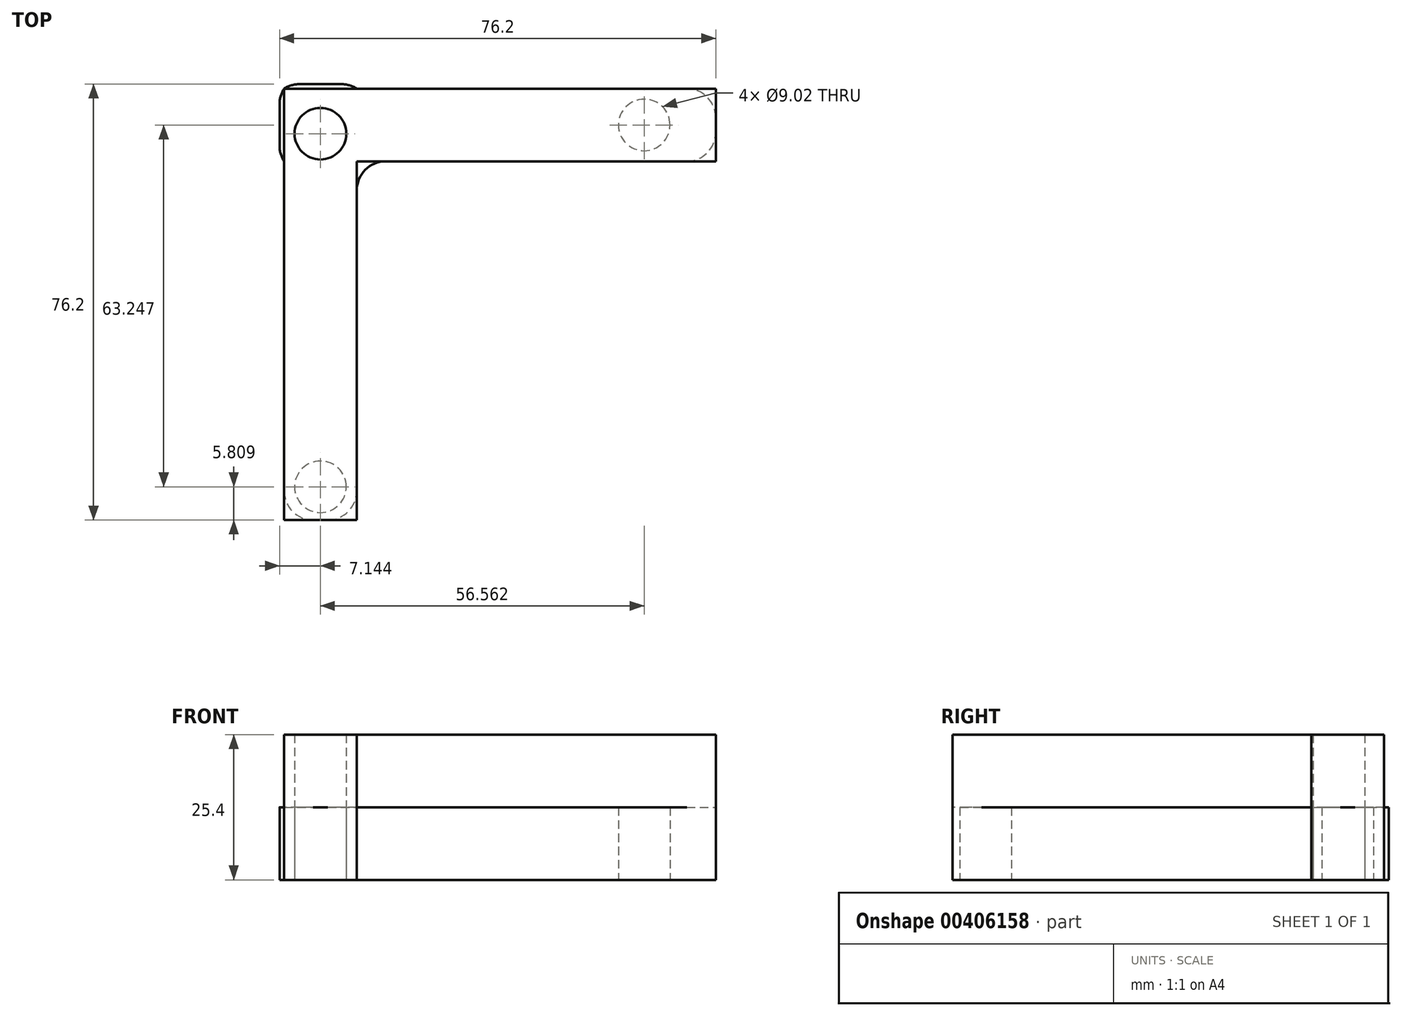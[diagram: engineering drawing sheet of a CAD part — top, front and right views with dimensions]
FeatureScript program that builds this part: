
annotation { "Feature Type Name" : "Feature", "Feature Type Description" : "" }
export const myFeature = defineFeature(function(context is Context, id is Id, definition is map)
    precondition{}
    {
        {
            var Q0;
            Q0=qCreatedBy(makeId("Top.planeOp"),FACE);
            var sketch = newSketch(context, id + "F0", { "sketchPlane" : qUnion([Q0])});
            skLineSegment(sketch, "E0.bottom", {"start": v(-24.6, -38.1) * mm, "end": v(-37.3, -38.1) * mm});
            skLineSegment(sketch, "E0.top", {"start": v(-24.6, 38.1) * mm, "end": v(-37.3, 38.1) * mm});
            skLineSegment(sketch, "E0.left", {"start": v(-24.6, -38.1) * mm, "end": v(-24.6, 24.6) * mm});
            skLineSegment(sketch, "E0.right", {"start": v(-37.3, -38.1) * mm, "end": v(-37.3, 38.1) * mm});
            skPoint(sketch, "E0.middle", {"position": v(-30.96, 0) * mm});
            skLineSegment(sketch, "E1.MirrorCS", {"start": v(38.1, 24.6) * mm, "end": v(-24.6, 24.6) * mm});
            skLineSegment(sketch, "E2.MirrorCS", {"start": v(-38.1, 24.6) * mm, "end": v(-38.1, 37.3) * mm});
            skLineSegment(sketch, "E3.MirrorCS", {"start": v(38.1, 24.6) * mm, "end": v(38.1, 37.3) * mm});
            skLineSegment(sketch, "E4.MirrorCS", {"start": v(38.1, 37.3) * mm, "end": v(-38.1, 37.3) * mm});
            skLineSegment(sketch, "E5.trimOffspring", {"start": v(-24.6, 37.3) * mm, "end": v(-24.6, 38.1) * mm});
            skLineSegment(sketch, "E6.trimOffspring", {"start": v(-37.3, 24.6) * mm, "end": v(-38.1, 24.6) * mm});
            skCircle(sketch, "E7", {"center": v(25.6, 30.96) * mm, "radius": 4.51 * mm});
            skPoint(sketch, "E7.centerSnap0", {"position": v(38.1, 30.96) * mm});
            skCircle(sketch, "E8.MirrorC", {"center": v(-30.96, 29.43) * mm, "radius": 4.51 * mm});
            skCircle(sketch, "E9.MirrorC", {"center": v(-30.96, -32.3) * mm, "radius": 4.51 * mm});
            skPoint(sketch, "E10", {"position": v(-30.96, -38.1) * mm});
            skSolve(sketch);
        }
        {
            var Q0;
            Q0=makeQuery(id+"F0.imprint","IMPRINT",FACE,{"disambiguationData":[TD([[makeQuery(id+"F0.imprint","IMPRINT",EDGE,{"derivedFrom":sQuery(id+"F0.wireOp",EDGE,"E8.MirrorC")}),-1.0]])]});
            var Q1;
            Q1=makeQuery(id+"F0.imprint","IMPRINT",FACE,{"disambiguationData":[TD([[makeQuery(id+"F0.imprint","IMPRINT",EDGE,{"derivedFrom":sQuery(id+"F0.wireOp",EDGE,"E7")}),1.0]])]});
            var Q2;
            Q2=makeQuery(id+"F0.imprint","IMPRINT",FACE,{"disambiguationData":[TD([[makeQuery(id+"F0.imprint","IMPRINT",EDGE,{"derivedFrom":sQuery(id+"F0.wireOp",EDGE,"E9.MirrorC")}),1.0]])]});
            var Q3;
            Q3=sQuery(id+"F0.wireOp",EDGE,"E7");
            var Q4;
            Q4=sQuery(id+"F0.wireOp",EDGE,"E8.MirrorC");
            var Q5;
            Q5=sQuery(id+"F0.wireOp",EDGE,"E9.MirrorC");
            extrude(context, id + "F1", {"entities" : qUnion([Q0, Q1, Q2]), "surfaceEntities" : qUnion([Q3, Q4, Q5]), "depth" : 25.4 * mm});
        }
        {
            var Q0;
            Q0 = qSketchRegion(id + "F0", true);
            extrude(context, id + "F2", {"entities" : qUnion([Q0]), "depth" : 12.7 * mm});
        }
        {
            var Q0;
            Q0=makeQuery(id+"F2.opExtrude","SWEPT_EDGE",EDGE,{"disambiguationData":[OSD([sQuery(id+"F0.wireOp",EDGE,"E0.bottom"),sQuery(id+"F0.wireOp",EDGE,"E0.right")])]});
            fillet(context, id + "F3", {"entities" : qUnion([Q0]), "radius" : 5.08 * mm, "tangentPropagation" : true, "allowEdgeOverflow" : false});
        }
        {
            var Q0;
            Q0=makeQuery(id+"F2.opExtrude","SWEPT_EDGE",EDGE,{"disambiguationData":[OSD([sQuery(id+"F0.wireOp",EDGE,"E1.MirrorCS"),sQuery(id+"F0.wireOp",EDGE,"E3.MirrorCS")])]});
            var Q1;
            Q1=makeQuery(id+"F2.opExtrude","SWEPT_EDGE",EDGE,{"disambiguationData":[OSD([sQuery(id+"F0.wireOp",EDGE,"E3.MirrorCS"),sQuery(id+"F0.wireOp",EDGE,"E4.MirrorCS")])]});
            var Q2;
            Q2=makeQuery(id+"F2.opExtrude","SWEPT_EDGE",EDGE,{"disambiguationData":[OSD([sQuery(id+"F0.wireOp",EDGE,"E0.bottom"),sQuery(id+"F0.wireOp",EDGE,"E0.left")])]});
            var Q3;
            Q3=makeQuery(id+"F2.opExtrude","SWEPT_EDGE",EDGE,{"disambiguationData":[OSD([sQuery(id+"F0.wireOp",EDGE,"E0.top"),sQuery(id+"F0.wireOp",EDGE,"E5.trimOffspring")])]});
            var Q4;
            Q4=makeQuery(id+"F2.opExtrude","SWEPT_EDGE",EDGE,{"disambiguationData":[OSD([sQuery(id+"F0.wireOp",EDGE,"E0.top"),sQuery(id+"F0.wireOp",EDGE,"E0.right")])]});
            var Q5;
            Q5=makeQuery(id+"F2.opExtrude","SWEPT_EDGE",EDGE,{"disambiguationData":[OSD([sQuery(id+"F0.wireOp",EDGE,"E2.MirrorCS"),sQuery(id+"F0.wireOp",EDGE,"E4.MirrorCS")])]});
            var Q6;
            Q6=makeQuery(id+"F2.opExtrude","SWEPT_EDGE",EDGE,{"disambiguationData":[OSD([sQuery(id+"F0.wireOp",EDGE,"E2.MirrorCS"),sQuery(id+"F0.wireOp",EDGE,"E6.trimOffspring")])]});
            var Q7;
            Q7=makeQuery(id+"F2.opExtrude","SWEPT_EDGE",EDGE,{"disambiguationData":[OSD([sQuery(id+"F0.wireOp",EDGE,"E0.left"),sQuery(id+"F0.wireOp",EDGE,"E1.MirrorCS")])]});
            fillet(context, id + "F4", {"entities" : qUnion([Q0, Q1, Q2, Q3, Q4, Q5, Q6, Q7]), "radius" : 5.08 * mm, "tangentPropagation" : true, "allowEdgeOverflow" : false});
        }
    });
